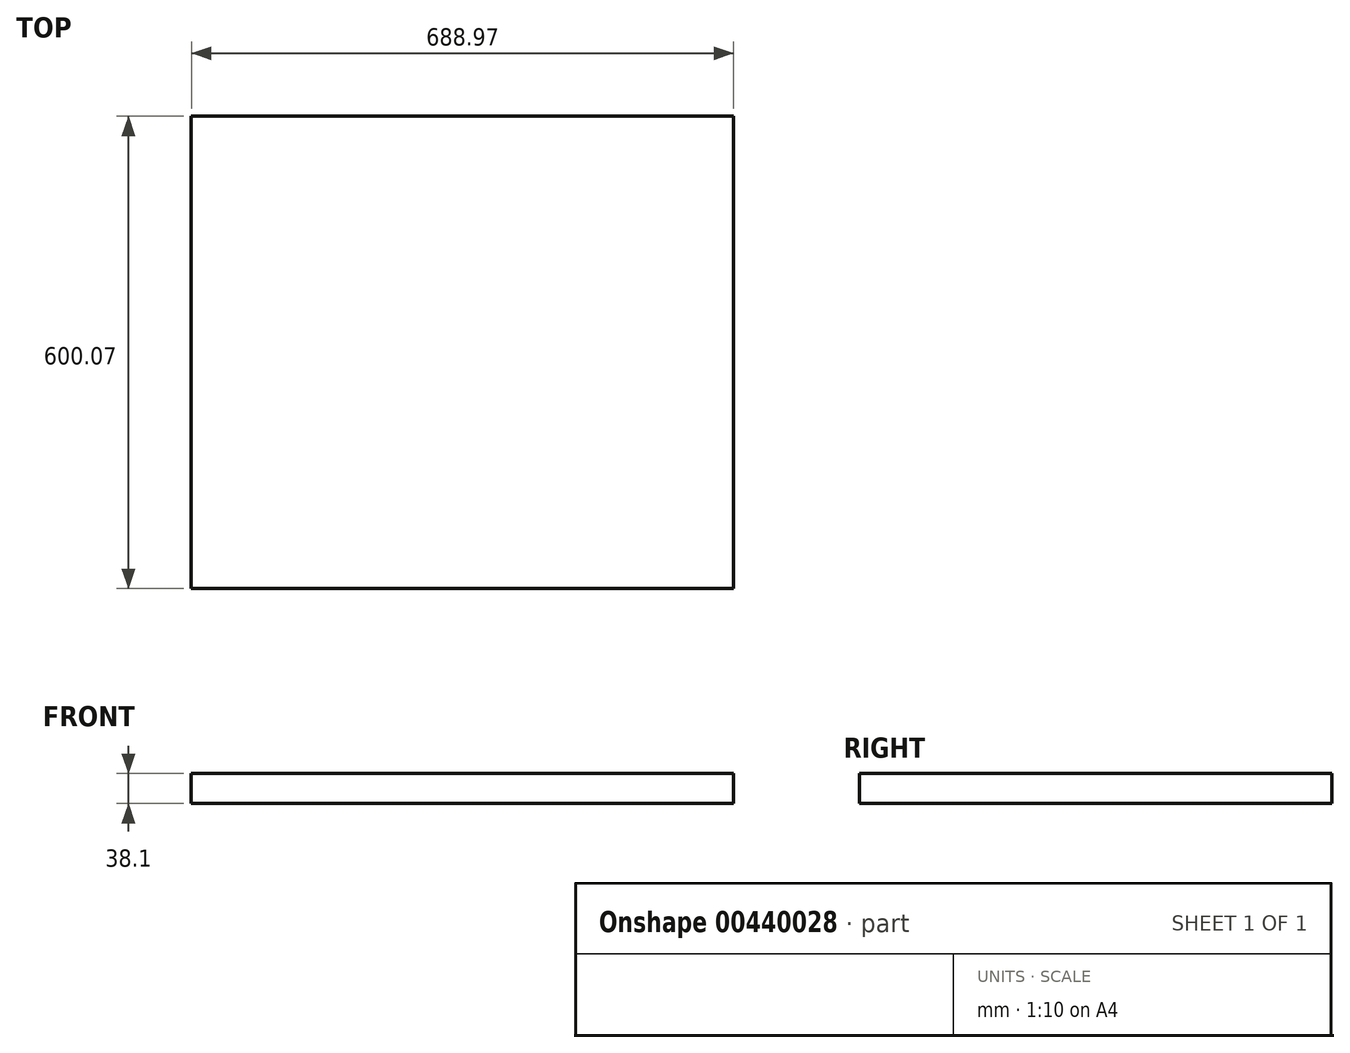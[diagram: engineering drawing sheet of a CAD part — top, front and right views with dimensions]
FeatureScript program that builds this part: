
annotation { "Feature Type Name" : "Feature", "Feature Type Description" : "" }
export const myFeature = defineFeature(function(context is Context, id is Id, definition is map)
    precondition{}
    {
        {
            var Q0;
            Q0=qCreatedBy(makeId("Top.planeOp"),FACE);
            var sketch = newSketch(context, id + "F0", { "sketchPlane" : qUnion([Q0])});
            skLineSegment(sketch, "E0.bottom", {"start": v(-346.27, 367.74) * mm, "end": v(342.7, 367.74) * mm});
            skLineSegment(sketch, "E0.top", {"start": v(-346.27, -232.33) * mm, "end": v(342.7, -232.33) * mm});
            skLineSegment(sketch, "E0.left", {"start": v(-346.27, 367.74) * mm, "end": v(-346.27, -232.33) * mm});
            skLineSegment(sketch, "E0.right", {"start": v(342.7, 367.74) * mm, "end": v(342.7, -232.33) * mm});
            skLineSegment(sketch, "E1.bottom", {"start": v(-346.27, -232.33) * mm, "end": v(342.7, -232.33) * mm, "construction": true});
            skLineSegment(sketch, "E1.top", {"start": v(-346.27, -54.53) * mm, "end": v(342.7, -54.53) * mm, "construction": true});
            skLineSegment(sketch, "E1.left", {"start": v(-346.27, -232.33) * mm, "end": v(-346.27, -54.53) * mm, "construction": true});
            skLineSegment(sketch, "E1.right", {"start": v(342.7, -232.33) * mm, "end": v(342.7, -54.53) * mm, "construction": true});
            skLineSegment(sketch, "E2.top", {"start": v(-346.27, 123.27) * mm, "end": v(342.7, 123.27) * mm, "construction": true});
            skLineSegment(sketch, "E2.left", {"start": v(-346.27, -54.53) * mm, "end": v(-346.27, 123.27) * mm, "construction": true});
            skLineSegment(sketch, "E2.right", {"start": v(342.7, -54.53) * mm, "end": v(342.7, 123.27) * mm, "construction": true});
            skLineSegment(sketch, "E3.bottom", {"start": v(-346.27, 123.27) * mm, "end": v(342.7, 123.27) * mm});
            skLineSegment(sketch, "E3.top", {"start": v(-346.27, 301.07) * mm, "end": v(342.7, 301.07) * mm});
            skLineSegment(sketch, "E3.left", {"start": v(-346.27, 123.27) * mm, "end": v(-346.27, 301.07) * mm});
            skLineSegment(sketch, "E3.right", {"start": v(342.7, 123.27) * mm, "end": v(342.7, 301.07) * mm});
            skSolve(sketch);
        }
        {
            var Q0;
            Q0 = qSketchRegion(id + "F0", true);
            extrude(context, id + "F1", {"entities" : qUnion([Q0]), "depth" : 38.1 * mm});
        }
    });
